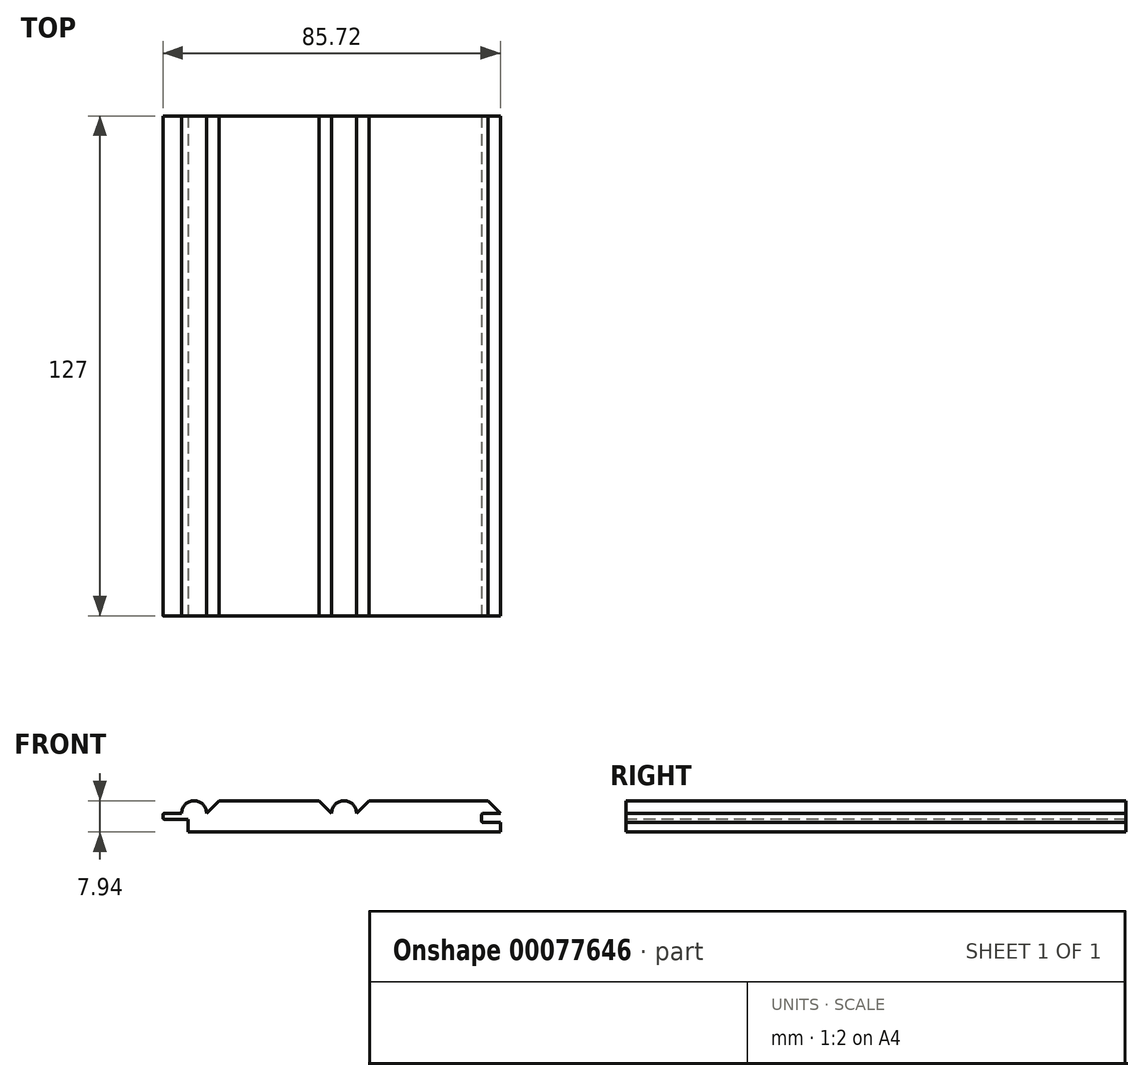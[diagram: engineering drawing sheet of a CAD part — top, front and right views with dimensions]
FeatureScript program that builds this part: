
annotation { "Feature Type Name" : "Feature", "Feature Type Description" : "" }
export const myFeature = defineFeature(function(context is Context, id is Id, definition is map)
    precondition{}
    {
        {
            var Q0;
            Q0=qCreatedBy(makeId("Front.planeOp"),FACE);
            var sketch = newSketch(context, id + "F0", { "sketchPlane" : qUnion([Q0])});
            skLineSegment(sketch, "E0", {"start": v(-36.51, -3.97) * mm, "end": v(42.86, -3.97) * mm});
            skLineSegment(sketch, "E1", {"start": v(42.86, -3.97) * mm, "end": v(42.86, -1.59) * mm});
            skLineSegment(sketch, "E2", {"start": v(39.69, 3.97) * mm, "end": v(9.52, 3.97) * mm});
            skLineSegment(sketch, "E3", {"start": v(-42.86, 0.29) * mm, "end": v(-42.86, -0.29) * mm});
            skLineSegment(sketch, "E4", {"start": v(-36.51, -3.97) * mm, "end": v(-36.51, -0.8) * mm});
            skLineSegment(sketch, "E5", {"start": v(-42.35, -0.8) * mm, "end": v(-36.51, -0.8) * mm});
            skLineSegment(sketch, "E6", {"start": v(-42.35, 0.8) * mm, "end": v(-38.1, 0.8) * mm});
            skArc(sketch, "E7", {"start": v(-42.86, -0.29) * mm, "mid": v(-42.71, -0.64) * mm, "end": v(-42.35, -0.8) * mm});
            skArc(sketch, "E8", {"start": v(-42.35, 0.8) * mm, "mid": v(-42.71, 0.64) * mm, "end": v(-42.86, 0.29) * mm});
            skArc(sketch, "E9", {"start": v(-34.93, 3.97) * mm, "mid": v(-37.17, 3.04) * mm, "end": v(-38.1, 0.8) * mm});
            skArc(sketch, "E10", {"start": v(-31.75, 0.8) * mm, "mid": v(-32.68, 3.04) * mm, "end": v(-34.93, 3.97) * mm});
            skLineSegment(sketch, "E11", {"start": v(-31.75, 0.8) * mm, "end": v(-28.58, 3.97) * mm});
            skArc(sketch, "E12", {"start": v(6.35, 0.8) * mm, "mid": v(5.42, 3.04) * mm, "end": v(3.18, 3.97) * mm});
            skArc(sketch, "E13", {"start": v(3.18, 3.97) * mm, "mid": v(0.93, 3.04) * mm, "end": v(0, 0.8) * mm});
            skLineSegment(sketch, "E14", {"start": v(0, 0.8) * mm, "end": v(-3.18, 3.97) * mm});
            skLineSegment(sketch, "E15", {"start": v(-3.18, 3.97) * mm, "end": v(-28.58, 3.97) * mm});
            skLineSegment(sketch, "E16", {"start": v(6.35, 0.8) * mm, "end": v(9.52, 3.97) * mm});
            skLineSegment(sketch, "E17", {"start": v(42.86, 0.8) * mm, "end": v(39.69, 3.97) * mm});
            skLineSegment(sketch, "E18", {"start": v(38.6, -1.59) * mm, "end": v(42.86, -1.59) * mm});
            skLineSegment(sketch, "E19", {"start": v(38.6, 0.8) * mm, "end": v(42.86, 0.8) * mm});
            skLineSegment(sketch, "E20", {"start": v(38.1, 0.29) * mm, "end": v(38.1, -1.08) * mm});
            skArc(sketch, "E21", {"start": v(38.6, 0.8) * mm, "mid": v(38.25, 0.64) * mm, "end": v(38.1, 0.29) * mm});
            skArc(sketch, "E22", {"start": v(38.1, -1.08) * mm, "mid": v(38.25, -1.44) * mm, "end": v(38.6, -1.59) * mm});
            skSolve(sketch);
        }
        {
            var Q0;
            Q0=makeQuery(id+"F0.imprint","IMPRINT",FACE,{"disambiguationData":[TD([[makeQuery(id+"F0.imprint","IMPRINT",EDGE,{"derivedFrom":sQuery(id+"F0.wireOp",EDGE,"E0")}),1.0]])]});
            extrude(context, id + "F1", {"entities" : qUnion([Q0]), "oppositeDirection" : true, "depth" : 127 * mm});
        }
    });
